# Revit family: Tables-Casual-Naughtone-Riley
name_source: partatom
category: Furniture
revit_build: Autodesk Revit Architecture 2014 (Build: 20140709_2115(x64)
units: mm (PartAtom-declared; Revit-internal decimal feet)

## types (1)
- Riley Laptop Table
    AssetIdentifier = RLY
    Barcode = 0
    COBie Description = Riley is a beautifully crafted solid oak pull-up table,
sized perfectly to slide over benches, sofa arms or chair
arms. The riley is available with an optional lino insert
and handy routed slots for pens, pencils and cups.
    Cost = 0 $
    Current Revision = 1
    Depth = 550 mm
    Description = Riley Table
    Height = 650 mm  [stored 2.13255 ft]
    Length = 450 mm  [stored 1.47638 ft]
    Manufacturer = Naughtone
    Material Frame = Laminate-Gen-Maple-Smooth_90
    Material Legs = Laminate-Gen-Maple-Smooth
    Model = Riley Table
    Name = Furniture-Table-Casual-Riley_Table
    Product Code = RLY
    Product URL = http://www.naughtone.com
    SerialNumber = 0
    TagNumber = 0
    TypeName = 450mm550mmx650mm Riley Table
    URL = http://www.naughtone.com
    Uniclass = Pr_40_50_21
    WarrantyDuration = 60

note: [stored X ft] marks values corroborated as IEEE doubles in the binary element streams (Revit-internal decimal feet)

## geometry (parser evidence)
native form markers: Sweep x1
no freeform markers — native parametric forms only
